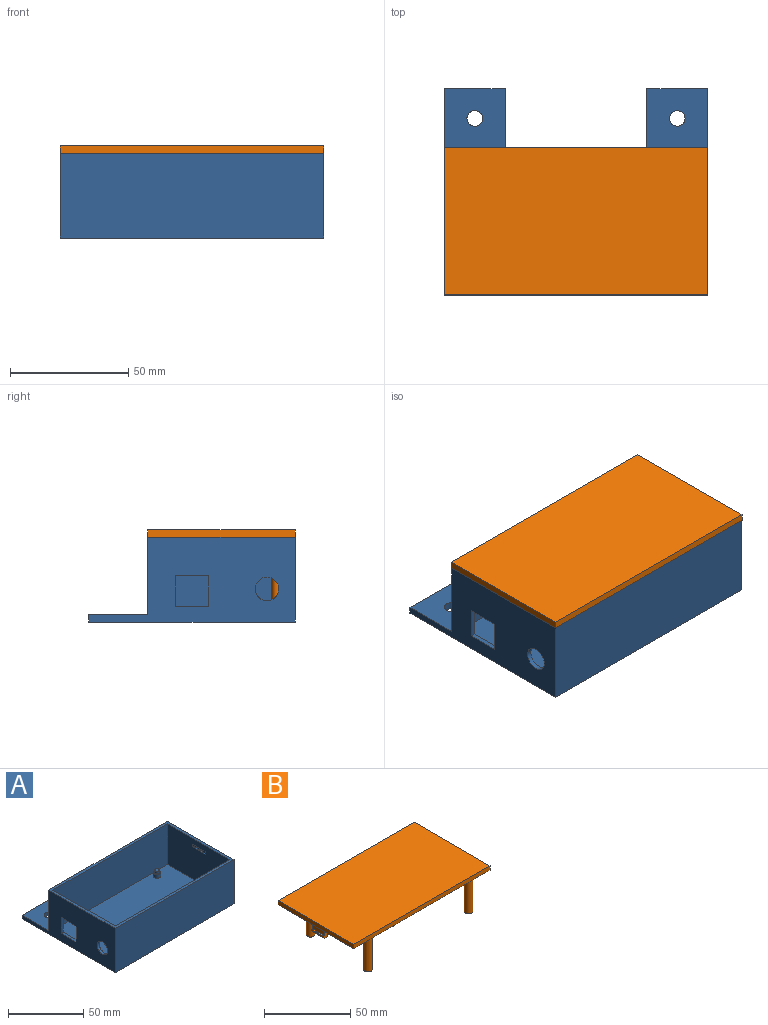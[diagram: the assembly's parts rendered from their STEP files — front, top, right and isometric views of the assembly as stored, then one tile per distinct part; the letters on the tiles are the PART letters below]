
ASSEMBLY  parts=2 mates=1
PART A: 50 faces, bbox 111.6x87.3x36 mm
  f0: plane 58.34x33mm, normal (1,0,0), area 1639.5mm2, adj f2,f11,f13,f14,f25,f26,f27,f28
  f1: plane 87.34x36mm, normal (-1,0,0), area 2058.7mm2, adj f14,f15,f17,f19,f23,f24,f25,f26
  f2: plane 107.6x58.34mm, normal (0,0,1), area 6198.8mm2, adj f0,f3,f5,f7,f9,f11,f12,f13
  f3: cylinder r=2.5mm len=5mm, axis (0,0,-1), area 47.1mm2, adj f2,f4
  f4: plane 5x5mm, normal (0,0,1), area 12.6mm2, adj f3,f40
  f5: cylinder r=2.5mm len=5mm, axis (0,0,-1), area 47.1mm2, adj f2,f6
  f6: plane 5x5mm, normal (0,0,1), area 12.6mm2, adj f5,f42
  f7: cylinder r=2.5mm len=5mm, axis (0,0,-1), area 47.1mm2, adj f2,f8
  f8: plane 5x5mm, normal (0,0,1), area 12.6mm2, adj f7,f44
  f9: cylinder r=2.5mm len=5mm, axis (0,0,-1), area 47.1mm2, adj f2,f10
  f10: plane 5x5mm, normal (0,0,1), area 12.6mm2, adj f9,f46
  f11: plane 107.6x33mm, normal (0,-1,0), area 3550.8mm2, adj f0,f2,f12,f14
  f12: plane 58.34x33mm, normal (-1,0,0), area 1900mm2, adj f2,f11,f13,f14,f30,f32,f33,f34
  f13: plane 107.6x33mm, normal (0,1,0), area 3550.8mm2, adj f0,f2,f12,f14
  f14: plane 111.6x62.34mm, normal (0,0,1), area 679.8mm2, adj f0,f1,f11,f12,f13,f19,f22,f23
  f15: plane 25.8x3mm, normal (0,1,0), area 77.4mm2, adj f1,f16,f17,f24
  f16: plane 25x3mm, normal (1,0,0), area 75mm2, adj f15,f17,f19,f24
  f17: plane 111.6x87.34mm, normal (0,0,-1), area 8178.7mm2, adj f1,f15,f16,f18,f19,f20,f22,f23
  f18: plane 25.8x3mm, normal (0,1,0), area 77.4mm2, adj f17,f20,f21,f22
  f19: plane 111.6x36mm, normal (0,1,0), area 3862.8mm2, adj f1,f14,f16,f17,f20,f21,f22,f24
  f20: plane 25x3mm, normal (-1,0,0), area 75mm2, adj f17,f18,f19,f21
  f21: plane 25.8x25mm, normal (0,0,1), area 610.8mm2, adj f18,f19,f20,f22,f49
  f22: plane 87.34x36mm, normal (1,0,0), area 2319.2mm2, adj f14,f17,f18,f19,f21,f23
  f23: plane 111.6x36mm, normal (0,-1,0), area 4017.6mm2, adj f1,f14,f17,f22
  f24: plane 25.8x25mm, normal (0,0,1), area 610.8mm2, adj f1,f15,f16,f19,f48
  f25: cylinder r=5mm len=10mm, axis (-1,0,0), area 62.8mm2, adj f0,f1
  f26: plane 13x2mm, normal (0,-1,0), area 26mm2, adj f0,f1,f27,f29
  f27: plane 14x2mm, normal (0,0,1), area 28mm2, adj f0,f1,f26,f28
  f28: plane 13x2mm, normal (0,1,0), area 26mm2, adj f0,f1,f27,f29
  f29: plane 14x2mm, normal (0,0,-1), area 28mm2, adj f0,f1,f26,f28
  f30: plane 12x1mm, normal (0,0,1), area 12mm2, adj f12,f31,f33,f34
  f31: plane 12x2.1mm, normal (-1,0,0), area 25.2mm2, adj f30,f32,f33,f34
  f32: plane 12x1mm, normal (0,0,-1), area 12mm2, adj f12,f31,f33,f34
  f33: plane 2.1x1mm, normal (0,-1,0), area 2.1mm2, adj f12,f30,f31,f32
  f34: plane 2.1x1mm, normal (0,1,0), area 2.1mm2, adj f12,f30,f31,f32
  f35: plane 12x1mm, normal (0,0,-1), area 12mm2, adj f0,f36,f38,f39
  f36: plane 12x2.1mm, normal (1,0,0), area 25.2mm2, adj f35,f37,f38,f39
  f37: plane 12x1mm, normal (0,0,1), area 12mm2, adj f0,f36,f38,f39
  f38: plane 2.1x1mm, normal (0,-1,0), area 2.1mm2, adj f0,f35,f36,f37
  f39: plane 2.1x1mm, normal (0,1,0), area 2.1mm2, adj f0,f35,f36,f37
  f40: cylinder r=1.5mm len=3mm, axis (0,0,-1), area 18.8mm2, adj f4,f41
  f41: plane 3x3mm, normal (0,0,1), area 7.1mm2, adj f40
  f42: cylinder r=1.5mm len=3mm, axis (0,0,-1), area 18.8mm2, adj f6,f43
  f43: plane 3x3mm, normal (0,0,1), area 7.1mm2, adj f42
  f44: cylinder r=1.5mm len=3mm, axis (0,0,-1), area 18.8mm2, adj f8,f45
  f45: plane 3x3mm, normal (0,0,1), area 7.1mm2, adj f44
  f46: cylinder r=1.5mm len=3mm, axis (0,0,-1), area 18.8mm2, adj f10,f47
  f47: plane 3x3mm, normal (0,0,1), area 7.1mm2, adj f46
  f48: cylinder r=3.3mm len=6.6mm, axis (0,0,1), area 62.2mm2, adj f17,f24
  f49: cylinder r=3.3mm len=6.6mm, axis (0,0,1), area 62.2mm2, adj f17,f21
PART B: 50 faces, bbox 111.6x62.3x31 mm
  f0: plane 111.6x62.34mm, normal (0,0,-1), area 6748.6mm2, adj f1,f2,f3,f4,f10,f11,f12,f13
  f1: plane 111.6x3mm, normal (0,1,0), area 334.8mm2, adj f0,f2,f4,f5
  f2: plane 62.34x3mm, normal (-1,0,0), area 187mm2, adj f0,f1,f3,f5
  f3: plane 111.6x3mm, normal (0,-1,0), area 334.8mm2, adj f0,f2,f4,f5
  f4: plane 62.34x3mm, normal (1,0,0), area 187mm2, adj f0,f1,f3,f5
  f5: plane 111.6x62.34mm, normal (0,0,1), area 6957.1mm2, adj f1,f2,f3,f4
  f6: plane 10x2.5mm, normal (0,0,-1), area 25mm2, adj f7,f11,f12,f13
  f7: plane 10x1mm, normal (0.71,0,-0.71), area 14.1mm2, adj f6,f8,f12,f13
  f8: plane 10x1mm, normal (1,0,0), area 10mm2, adj f7,f9,f12,f13
  f9: plane 10x1mm, normal (0,0,1), area 10mm2, adj f8,f10,f12,f13
  f10: plane 10x5mm, normal (1,0,0), area 50mm2, adj f0,f9,f12,f13
  f11: plane 10x7mm, normal (-1,0,0), area 70mm2, adj f0,f6,f12,f13
  f12: plane 7x3.5mm, normal (0,-1,0), area 19mm2, adj f0,f6,f7,f8,f9,f10,f11
  f13: plane 7x3.5mm, normal (0,1,0), area 19mm2, adj f0,f6,f7,f8,f9,f10,f11
  f14: plane 10x5mm, normal (-1,0,0), area 50mm2, adj f0,f15,f20,f21
  f15: plane 10x1mm, normal (0,0,1), area 10mm2, adj f14,f16,f20,f21
  f16: plane 10x1mm, normal (-1,0,0), area 10mm2, adj f15,f17,f20,f21
  f17: plane 10x1mm, normal (-0.71,0,-0.71), area 14.1mm2, adj f16,f18,f20,f21
  f18: plane 10x2.5mm, normal (0,0,-1), area 25mm2, adj f17,f19,f20,f21
  f19: plane 10x7mm, normal (1,0,0), area 70mm2, adj f0,f18,f20,f21
  f20: plane 7x3.5mm, normal (0,-1,0), area 19mm2, adj f0,f14,f15,f16,f17,f18,f19
  f21: plane 7x3.5mm, normal (0,1,0), area 19mm2, adj f0,f14,f15,f16,f17,f18,f19
  f22: plane 2x2mm, normal (-1,0,0), area 4mm2, adj f0,f23,f25,f26
  f23: plane 10x2mm, normal (0,-1,0), area 20mm2, adj f0,f22,f24,f26
  f24: plane 2x2mm, normal (1,0,0), area 4mm2, adj f0,f23,f25,f26
  f25: plane 10x2mm, normal (0,1,0), area 20mm2, adj f0,f22,f24,f26
  f26: plane 10x2mm, normal (0,0,-1), area 20mm2, adj f22,f23,f24,f25
  f27: plane 2x2mm, normal (-1,0,0), area 4mm2, adj f0,f28,f30,f31
  f28: plane 10x2mm, normal (0,-1,0), area 20mm2, adj f0,f27,f29,f31
  f29: plane 2x2mm, normal (1,0,0), area 4mm2, adj f0,f28,f30,f31
  f30: plane 10x2mm, normal (0,1,0), area 20mm2, adj f0,f27,f29,f31
  f31: plane 10x2mm, normal (0,0,-1), area 20mm2, adj f27,f28,f29,f30
  f32: plane 2x2mm, normal (1,0,0), area 4mm2, adj f0,f33,f35,f36
  f33: plane 10x2mm, normal (0,1,0), area 20mm2, adj f0,f32,f34,f36
  f34: plane 2x2mm, normal (-1,0,0), area 4mm2, adj f0,f33,f35,f36
  f35: plane 10x2mm, normal (0,-1,0), area 20mm2, adj f0,f32,f34,f36
  f36: plane 10x2mm, normal (0,0,-1), area 20mm2, adj f32,f33,f34,f35
  f37: plane 2x2mm, normal (-1,0,0), area 4mm2, adj f0,f38,f40,f41
  f38: plane 10x2mm, normal (0,-1,0), area 20mm2, adj f0,f37,f39,f41
  f39: plane 2x2mm, normal (1,0,0), area 4mm2, adj f0,f38,f40,f41
  f40: plane 10x2mm, normal (0,1,0), area 20mm2, adj f0,f37,f39,f41
  f41: plane 10x2mm, normal (0,0,-1), area 20mm2, adj f37,f38,f39,f40
  f42: plane 5x5mm, normal (0,0,-1), area 19.6mm2, adj f43
  f43: cylinder r=2.5mm len=28mm, axis (0,0,1), area 439.8mm2, adj f0,f42
  f44: plane 5x5mm, normal (0,0,-1), area 19.6mm2, adj f45
  f45: cylinder r=2.5mm len=28mm, axis (0,0,1), area 439.8mm2, adj f0,f44
  f46: plane 5x5mm, normal (0,0,-1), area 19.6mm2, adj f47
  f47: cylinder r=2.5mm len=28mm, axis (0,0,1), area 439.8mm2, adj f0,f46
  f48: plane 5x5mm, normal (0,0,-1), area 19.6mm2, adj f49
  f49: cylinder r=2.5mm len=28mm, axis (0,0,1), area 439.8mm2, adj f0,f48
PLACE A t=(-26.17,7.02,13.32)mm
PLACE B t=(-59.08,-3.15,46.32)mm
MATE fastened A.f14 <-> B.f0  axis (0,0,1) through (-93.82,33.71,46.32)mm
